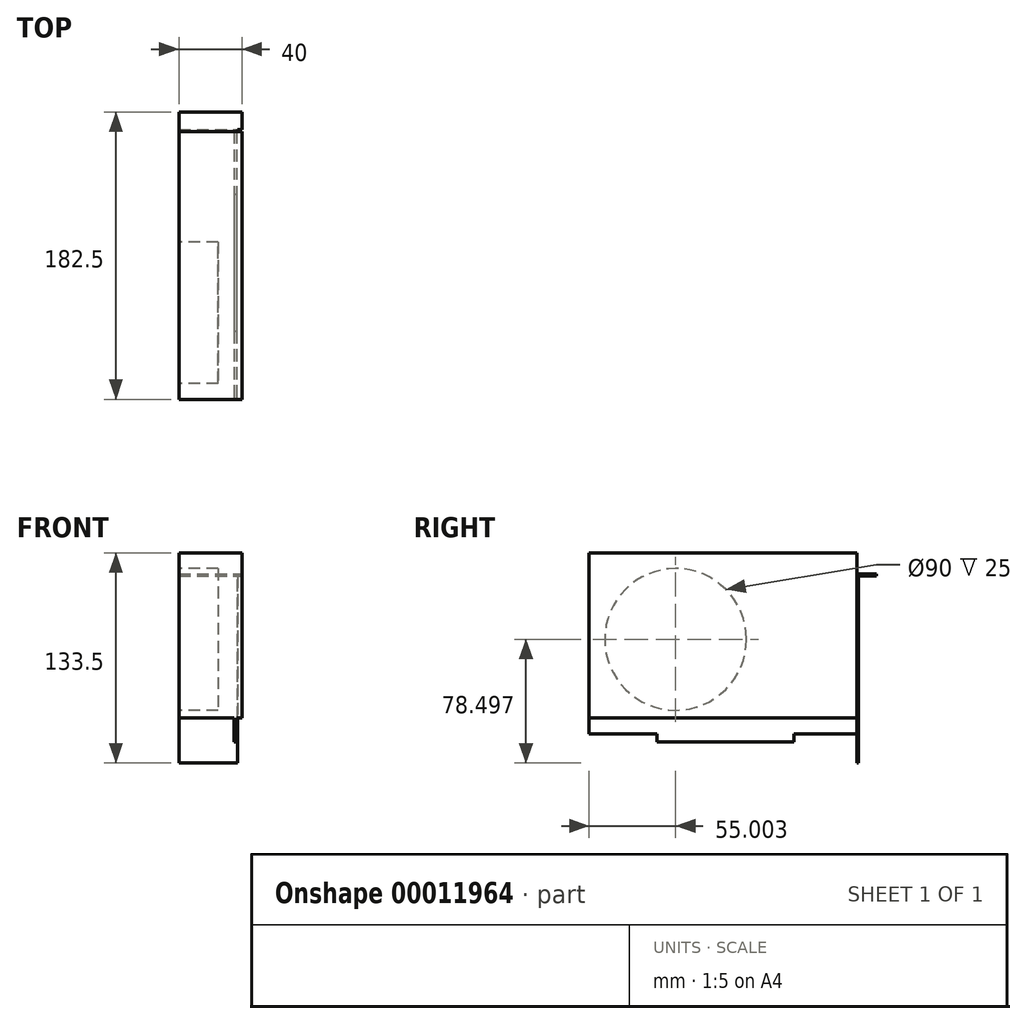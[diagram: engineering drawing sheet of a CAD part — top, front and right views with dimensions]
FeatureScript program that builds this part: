
annotation { "Feature Type Name" : "Feature", "Feature Type Description" : "" }
export const myFeature = defineFeature(function(context is Context, id is Id, definition is map)
    precondition{}
    {
        {
            var Q0;
            Q0=qCreatedBy(makeId("Right.planeOp"),FACE);
            var sketch = newSketch(context, id + "F0", { "sketchPlane" : qUnion([Q0])});
            skLineSegment(sketch, "E0.bottom", {"start": v(68.35, 45) * mm, "end": v(-101.65, 45) * mm});
            skLineSegment(sketch, "E0.top", {"start": v(68.35, -60) * mm, "end": v(-101.65, -60) * mm});
            skLineSegment(sketch, "E0.left", {"start": v(68.35, 45) * mm, "end": v(68.35, -60) * mm});
            skLineSegment(sketch, "E0.right", {"start": v(-101.65, 45) * mm, "end": v(-101.65, -60) * mm});
            skSolve(sketch);
        }
        {
            var Q0;
            Q0=makeQuery(id+"F0.imprint","IMPRINT",FACE,{"disambiguationData":[TD([[makeQuery(id+"F0.imprint","IMPRINT",EDGE,{"derivedFrom":sQuery(id+"F0.wireOp",EDGE,"E0.bottom")}),1.0]])]});
            extrude(context, id + "F1", {"entities" : qUnion([Q0]), "depth" : 40 * mm});
        }
        {
            var Q0;
            Q0=makeQuery(id+"F1.opExtrude","SWEPT_FACE",FACE,{"disambiguationData":[OSD([sQuery(id+"F0.wireOp",EDGE,"E0.top")])]});
            var sketch = newSketch(context, id + "F2", { "sketchPlane" : qUnion([Q0])});
            skLineSegment(sketch, "E1", {"start": v(40, -68.35) * mm, "end": v(36.5, -68.35) * mm, "construction": true});
            skLineSegment(sketch, "E2.bottom", {"start": v(36.5, -68.35) * mm, "end": v(35, -68.35) * mm});
            skLineSegment(sketch, "E2.top", {"start": v(36.5, 101.65) * mm, "end": v(35, 101.65) * mm});
            skLineSegment(sketch, "E2.left", {"start": v(36.5, -68.35) * mm, "end": v(36.5, 101.65) * mm});
            skLineSegment(sketch, "E2.right", {"start": v(35, -68.35) * mm, "end": v(35, 101.65) * mm});
            skSolve(sketch);
        }
        {
            var Q0;
            Q0=makeQuery(id+"F2.imprint","IMPRINT",FACE,{"disambiguationData":[TD([[makeQuery(id+"F2.imprint","IMPRINT",EDGE,{"derivedFrom":sQuery(id+"F2.wireOp",EDGE,"E2.bottom")}),-1.0]])]});
            extrude(context, id + "F3", {"entities" : qUnion([Q0]), "operationType" : NewBodyOperationType.ADD, "depth" : 10 * mm});
        }
        {
            var Q0;
            Q0=makeQuery(id+"F3.opExtrude","CAP_FACE",FACE,{"disambiguationData":[OSD([sQuery(id+"F2.wireOp",EDGE,"E2.bottom"),sQuery(id+"F2.wireOp",EDGE,"E2.top"),sQuery(id+"F2.wireOp",EDGE,"E2.left"),sQuery(id+"F2.wireOp",EDGE,"E2.right")])],"isStart":false});
            var sketch = newSketch(context, id + "F4", { "sketchPlane" : qUnion([Q0])});
            skLineSegment(sketch, "E3", {"start": v(36.5, -68.35) * mm, "end": v(36.5, -28.35) * mm, "construction": true});
            skLineSegment(sketch, "E4.bottom", {"start": v(36.5, -28.35) * mm, "end": v(35, -28.35) * mm});
            skLineSegment(sketch, "E4.top", {"start": v(36.5, 58.65) * mm, "end": v(35, 58.65) * mm});
            skLineSegment(sketch, "E4.left", {"start": v(36.5, -28.35) * mm, "end": v(36.5, 58.65) * mm});
            skLineSegment(sketch, "E4.right", {"start": v(35, -28.35) * mm, "end": v(35, 58.65) * mm});
            skSolve(sketch);
        }
        {
            var Q0;
            Q0=makeQuery(id+"F4.imprint","IMPRINT",FACE,{"disambiguationData":[TD([[makeQuery(id+"F4.imprint","IMPRINT",EDGE,{"derivedFrom":sQuery(id+"F4.wireOp",EDGE,"E4.bottom")}),-1.0]])]});
            extrude(context, id + "F5", {"entities" : qUnion([Q0]), "operationType" : NewBodyOperationType.ADD, "depth" : 5 * mm});
        }
        {
            var Q0;
            Q0=makeQuery(id+"F3.boolean.opBoolean","MERGE",FACE,{"derivedFrom":[makeQuery(id+"F1.opExtrude","SWEPT_FACE",FACE,{"disambiguationData":[OSD([sQuery(id+"F0.wireOp",EDGE,"E0.left")])]}),makeQuery(id+"F3.opExtrude","SWEPT_FACE",FACE,{"disambiguationData":[OSD([sQuery(id+"F2.wireOp",EDGE,"E2.bottom")])]})]});
            var sketch = newSketch(context, id + "F6", { "sketchPlane" : qUnion([Q0])});
            skLineSegment(sketch, "E5", {"start": v(0, 45) * mm, "end": v(0, 31.5) * mm, "construction": true});
            skLineSegment(sketch, "E6.bottom", {"start": v(0, 31.5) * mm, "end": v(-40, 31.5) * mm});
            skLineSegment(sketch, "E6.top", {"start": v(0, -88.5) * mm, "end": v(-40, -88.5) * mm});
            skLineSegment(sketch, "E6.left", {"start": v(0, 31.5) * mm, "end": v(0, -88.5) * mm});
            skLineSegment(sketch, "E6.right", {"start": v(-40, 31.5) * mm, "end": v(-40, -88.5) * mm});
            skSolve(sketch);
        }
        {
            var Q0;
            {var subQ14=sQuery(id+"F6.wireOp",EDGE,"E6.bottom");Q0=makeQuery(id+"F6.imprint","IMPRINT",FACE,{"disambiguationData":[TD([[makeQuery(id+"F6.imprint","IMPRINT",EDGE,{"derivedFrom":subQ14}),1.0]])]});}
            var Q1;
            {var subQ14=sQuery(id+"F6.wireOp",EDGE,"E6.top");Q1=makeQuery(id+"F6.imprint","IMPRINT",FACE,{"disambiguationData":[TD([[makeQuery(id+"F6.imprint","IMPRINT",EDGE,{"derivedFrom":subQ14}),-1.0]])]});}
            extrude(context, id + "F7", {"entities" : qUnion([Q0, Q1]), "operationType" : NewBodyOperationType.ADD, "depth" : 12.5 * mm});
        }
        {
            var Q0;
            Q0=makeQuery(id+"F7.opExtrude","CAP_FACE",FACE,{"disambiguationData":[OSD([sQuery(id+"F6.wireOp",EDGE,"E6.bottom"),sQuery(id+"F6.wireOp",EDGE,"E6.top"),sQuery(id+"F6.wireOp",EDGE,"E6.left"),sQuery(id+"F6.wireOp",EDGE,"E6.right")])],"isStart":false});
            var sketch = newSketch(context, id + "F8", { "sketchPlane" : qUnion([Q0])});
            skLineSegment(sketch, "E7", {"start": v(0, 31.5) * mm, "end": v(0, 30.26) * mm, "construction": true});
            skLineSegment(sketch, "E8", {"start": v(0, 30.26) * mm, "end": v(-40, 30.26) * mm});
            skSolve(sketch);
        }
        {
            var Q0;
            {var subQ1=sQuery(id+"F8.wireOp",EDGE,"E8");Q0=makeQuery(id+"F8.imprint","IMPRINT",FACE,{"disambiguationData":[TD([[makeQuery(id+"F8.imprint","IMPRINT",EDGE,{"derivedFrom":subQ1}),1.0]])]});}
            extrude(context, id + "F9", {"entities" : qUnion([Q0]), "operationType" : NewBodyOperationType.REMOVE, "oppositeDirection" : true, "depth" : (12.5 - 1.25) * mm});
        }
        {
            var Q0;
            Q0=makeQuery(id+"F7.boolean.opBoolean","MERGE",FACE,{"derivedFrom":[makeQuery(id+"F1.opExtrude","CAP_FACE",FACE,{"disambiguationData":[OSD([sQuery(id+"F0.wireOp",EDGE,"E0.bottom"),sQuery(id+"F0.wireOp",EDGE,"E0.top"),sQuery(id+"F0.wireOp",EDGE,"E0.left"),sQuery(id+"F0.wireOp",EDGE,"E0.right")])],"isStart":false}),makeQuery(id+"F7.opExtrude","SWEPT_FACE",FACE,{"disambiguationData":[OSD([sQuery(id+"F6.wireOp",EDGE,"E6.right")])]})]});
            var sketch = newSketch(context, id + "F10", { "sketchPlane" : qUnion([Q0])});
            skLineSegment(sketch, "E9.bottom", {"start": v(69.6, -88.5) * mm, "end": v(68.35, -88.5) * mm});
            skLineSegment(sketch, "E9.top", {"start": v(69.6, 31.5) * mm, "end": v(68.35, 31.5) * mm});
            skLineSegment(sketch, "E9.left", {"start": v(69.6, -88.5) * mm, "end": v(69.6, 31.5) * mm});
            skLineSegment(sketch, "E9.right", {"start": v(68.35, -88.5) * mm, "end": v(68.35, 31.5) * mm});
            skSolve(sketch);
        }
        {
            var Q0;
            {var subQ2=sQuery(id+"F10.wireOp",EDGE,"E9.bottom");Q0=makeQuery(id+"F10.imprint","IMPRINT",FACE,{"disambiguationData":[TD([[makeQuery(id+"F10.imprint","IMPRINT",EDGE,{"derivedFrom":subQ2}),-1.0]])]});}
            extrude(context, id + "F11", {"entities" : qUnion([Q0]), "operationType" : NewBodyOperationType.REMOVE, "oppositeDirection" : true, "depth" : 2.75 * mm});
        }
        {
            var Q0;
            Q0=makeQuery(id+"F7.boolean.opBoolean","MERGE",FACE,{"derivedFrom":[makeQuery(id+"F1.opExtrude","CAP_FACE",FACE,{"disambiguationData":[OSD([sQuery(id+"F0.wireOp",EDGE,"E0.bottom"),sQuery(id+"F0.wireOp",EDGE,"E0.top"),sQuery(id+"F0.wireOp",EDGE,"E0.left"),sQuery(id+"F0.wireOp",EDGE,"E0.right")])],"isStart":true}),makeQuery(id+"F7.opExtrude","SWEPT_FACE",FACE,{"disambiguationData":[OSD([sQuery(id+"F6.wireOp",EDGE,"E6.left")])]})]});
            var sketch = newSketch(context, id + "F12", { "sketchPlane" : qUnion([Q0])});
            skLineSegment(sketch, "E10", {"start": v(101.65, 45) * mm, "end": v(46.65, 45) * mm, "construction": true});
            skLineSegment(sketch, "E11", {"start": v(46.65, 45) * mm, "end": v(46.65, -10) * mm, "construction": true});
            skCircle(sketch, "E12", {"center": v(46.65, -10) * mm, "radius": 45 * mm});
            skSolve(sketch);
        }
        {
            var Q0;
            Q0=makeQuery(id+"F12.imprint","IMPRINT",FACE,{"disambiguationData":[TD([[makeQuery(id+"F12.imprint","IMPRINT",EDGE,{"derivedFrom":sQuery(id+"F12.wireOp",EDGE,"E12")}),1.0]])]});
            extrude(context, id + "F13", {"entities" : qUnion([Q0]), "operationType" : NewBodyOperationType.REMOVE, "oppositeDirection" : true, "depth" : 25 * mm});
        }
    });
